# Revit family: 9-SKIRTBOARD-CADS-68-Skirtboard-1x10-4-REVIT_Versatex-Generic-Model-1in-x-10in-SKIRTBOARD
name_source: partatom
category: Generic Models
units: mm (PartAtom-declared; Revit-internal decimal feet)

## family parameters
Can host rebar = No
Cut with Voids When Loaded = No
Host = Face
Maintain Annotation Orientation = No
Part Type = Normal
Room Calculation Point = No
Round Connector Dimension = Use Diameter
Shared = No

## types (1)
- 9-SKIRTBOARD-CADS-68-Skirtboard-1x10-4-REVIT_Versatex-Generic-Model-1in-x-10in-SKIRTBOARD
    Default Elevation = 4' - 0"
    Description = NOMINAL 1" X 10" SKIRTBOARD
    Length = 4' - 0"
    Literature = https://versatex.com
    Manufacturer = Versatex
    Manufacturer Fax = 724-857-1171
    Manufacturer Website = https://versatex.com
    Material = Versatex PVC - Smooth
    Message Manufacturer = https://versatex.com
    Model = SSBSM/TR011018
    Sales Information = https://versatex.com
    Specification = https://www.arcat.com
    URL = https://versatex.com
    Warranty = https://versatex.com

## geometry (parser evidence)
native form markers: Blend x2, Sweep x1
no freeform markers — native parametric forms only
